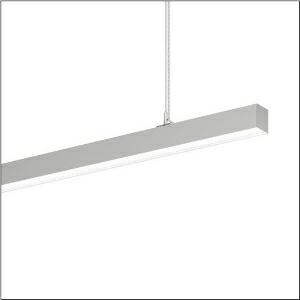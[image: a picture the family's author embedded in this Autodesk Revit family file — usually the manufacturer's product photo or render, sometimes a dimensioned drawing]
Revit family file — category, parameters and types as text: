
# Revit family: silica_21_51mx30da34sb
name_source: partatom
category: Lighting Fixtures
units: mm (PartAtom-declared; Revit-internal decimal feet)

## family parameters
Cut with Voids When Loaded = No
Host = Face
Light Source = No
Part Type = Normal
Room Calculation Point = No
Round Connector Dimension = Use Diameter
Shared = No

## types (1)
- --- (1 x LED, 4210 lm, 27.7 W, 3000K)
    Apparent Load = 28 VA
    CIE Flux Codes = 47 79 96 57 100
    Color Rendering = 80
    Color Temperature = 3000K
    Default Elevation = 1800 mm
    Description = Silica 21, office luminaire, primary optical cover: cover, of PMMA, opal, light emission: direct/indirect distribution, primary light characteristic: symmetric, installation type: suspended mounting, LED, rated luminous flux: 4.210lm, luminous efficacy: 152lm/W, light colour: 830, colour temperature: 3000K, control gear: DALI 2, with terminal, 3+2-pole, max. 2.5mm², mains connection: 220..240V, AC, 50/60Hz, rated input power: 27.7W, luminaire housing, of aluminium, metallic grey (RAL 9006), length: 1.204mm, width: 53mm, height: 53mm, protection rating (complete): IP20, insulation class (complete): insulation class I (protective earthing), certification: CE, permissible operating ambient temperature: 0..+35°C, standard: EN 50419, packaging unit: 1 piece
    Height = 53 mm
    Lamp = 1 x LED
    Lamp Light Flux = 4210 lm
    Lamp Power = 27.7 W
    Lamp count = 1
    Length = 1204 mm
    Luminous efficacy = 152 lm/W
    Manufacturer = Siteco
    ModVariant = No
    Model = 51MX30DA34SB
    Mounting Place = Ceiling
    Mounting Type = Pendant
    Number of Poles = 1
    OnlyDefault = Yes
    Power Factor = 1
    Product Name = Silica 21
    Product group = office luminaire | ceiling pendant
    ProductGroupID = 903
    Protection Class = Protection class I
    Protection Degree = IP 20
    RLX_Detail_Level = 1
    RLX_Emergency_Light_Flux = 0 lm
    RLX_Emergency_Type = 0
    RLX_Emergency_Type_DB = No
    RlxData = <blob elided: 23245 chars, md5=6f9f023a>
    Socket = socket
    Standby Power = 0 W
    System Light Flux = 4210 lm
    System Power = 28 W
    Type Comments = factory setting: luminous flux: 100 % | dim-lin: 254 | 233 mA
    Type Image = l_1335864.jpg
    URL = http://relux.com
    VarID = @adj_117313
    Voltage = 0 V
    Weight = 0.00 kg
    Width = 53 mm

## geometry (parser evidence)
native form markers: Blend x4, Sweep x12
no freeform markers — native parametric forms only
